# Revit family: TLI - Allegro W OMG - Wall
name_source: partatom
category: Lighting Fixtures
revit_build: Autodesk Revit Architecture 2012 (Build: 20110916_2132(x64)
units: mm (PartAtom-declared; Revit-internal decimal feet)

## types (6) — shared parameters
ADA Compliant = No
Amps = 1
Color Filter = 16777215
Conditions of Use = Elements are representations. Color and detail may differ from actual product. Information is for general use and should be reviewed by a Professional.
Depth = 0' - 5 1/2"
Description = Architectectural Outdoor
Diffuser = Luminous White Acrylic
Diffuser Material = Acrylic - TLI - Luminous White
Dimming Lamp Color Temperature Shift = <None>
Distributor Locations = USA, Canada, Puerto Rico
Fascia Material = Paint - TLI - Matte Silver
Finish = Textured Black
Fixture = Aluminum
Fixture Material = Paint - TLI - Textured Black
Industry Standards = Buy America Act
Integral Battery = No
Lamp Base = 4-Pin
Length = 1' - 9 1/8"
Manufacturer = Teron Lighting
Manufacturer Telephone = 01-513-858-6004
MasterFormat 2004 Number = 26.56.00
MasterFormat 2004 Title = Exterior Lighting
Mounting Type = 4" Junction Box
Photometric Web File = generic.ies
Point of Final Manufacture = Fairfield, OH, USA
Product = Allegro W OMG
Product Documentation URL = http://teronlighting.com
Product Page URL = http://teronlighting.com
Remote Battery = No
Requires Special Disposal = No
Tilt Angle = 0.00°
URL = http://teronlighting.com
Width = 0' - 9"
zero-valued in all types: Cost, Percentage Post-Consumer, Percentage Pre-Consumer

## per-type parameters (varying)
| type | Apparent Load | Lamp | Model | Number of Lamps | Voltage | Watts |
| Biax 4-Pin 2 -  27W - 120V | 54 VA | 2 - 27W BIAX | ALLW - OMG - F227E | 2 | 120 V | 54 W |
| Biax 4-Pin 2 -  27W - 277V | 54 VA | 2 - 27W BIAX | ALLW - OMG - F227E | 2 | 277 V | 54 W |
| Biax 4-Pin 1 -  39W - 120V | 39 VA | 1 - 39W BIAX | ALLW - OMG - F139E | 1 | 120 V | 39 W |
| Biax 4-Pin 1 -  39W - 277V | 39 VA | 1 - 39W BIAX | ALLW - OMG - F139E | 1 | 277 V | 39 W |
| Biax 4-Pin 2 -  39W - 120V | 78 VA | 2 - 39W BIAX | ALLW - OMG - F239E | 2 | 120 V | 78 W |
| Biax 4-Pin 2 -  39W - 177V | 78 VA | 2 - 39W BIAX | ALLW - OMG - F239E | 2 | 277 V | 78 W |

## geometry (parser evidence)
native form markers: Blend x16, Sweep x3
no freeform markers — native parametric forms only
